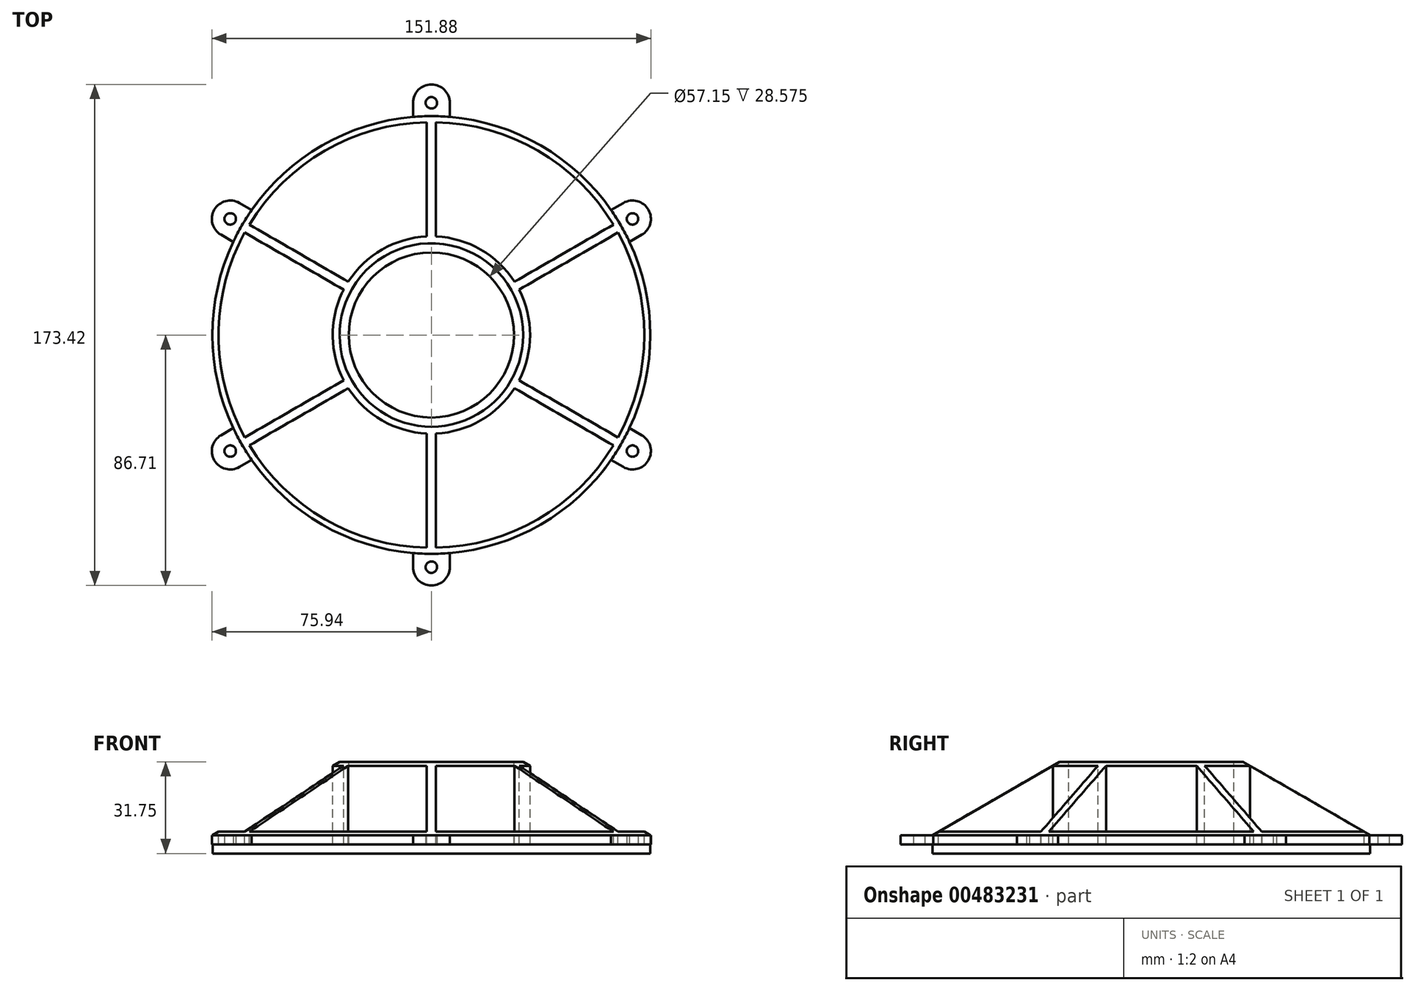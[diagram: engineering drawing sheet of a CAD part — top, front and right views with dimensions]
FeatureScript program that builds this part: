
annotation { "Feature Type Name" : "Feature", "Feature Type Description" : "" }
export const myFeature = defineFeature(function(context is Context, id is Id, definition is map)
    precondition{}
    {
        {
            var Q0;
            Q0=qCreatedBy(makeId("Top.planeOp"),FACE);
            var sketch = newSketch(context, id + "F0", { "sketchPlane" : qUnion([Q0])});
            skCircle(sketch, "E0", {"center": v(0, 0) * mm, "radius": 31.75 * mm});
            skSolve(sketch);
        }
        {
            var Q0;
            Q0 = qSketchRegion(id + "F0", true);
            extrude(context, id + "F1", {"entities" : qUnion([Q0]), "oppositeDirection" : true, "depth" : 25.4 * mm, "hasDraft" : true, "draftAngle" : 60 * degree});
        }
        {
            var Q0;
            Q0=makeQuery(id+"F1.opExtrude","CAP_FACE",FACE,{"disambiguationData":[OSD([sQuery(id+"F0.wireOp",EDGE,"E0")])],"isStart":false});
            var sketch = newSketch(context, id + "F2", { "sketchPlane" : qUnion([Q0])});
            skCircle(sketch, "E1", {"center": v(0, 0) * mm, "radius": 75.74 * mm});
            skSolve(sketch);
        }
        {
            var Q0;
            Q0 = qSketchRegion(id + "F2", true);
            extrude(context, id + "F3", {"entities" : qUnion([Q0]), "operationType" : NewBodyOperationType.ADD, "depth" : 3.17 * mm});
        }
        {
            var Q0;
            Q0=makeQuery(id+"F1.opExtrude","CAP_FACE",FACE,{"disambiguationData":[OSD([sQuery(id+"F0.wireOp",EDGE,"E0")])],"isStart":true});
            var sketch = newSketch(context, id + "F4", { "sketchPlane" : qUnion([Q0])});
            skCircle(sketch, "E2", {"center": v(0, 0) * mm, "radius": 28.58 * mm});
            skSolve(sketch);
        }
        {
            var Q0;
            Q0 = qSketchRegion(id + "F4", true);
            extrude(context, id + "F5", {"entities" : qUnion([Q0]), "operationType" : NewBodyOperationType.REMOVE, "endBound" : BoundingType.THROUGH_ALL, "oppositeDirection" : true, "depth" : 25.4 * mm});
        }
        {
            var Q0;
            Q0=qCreatedBy(makeId("Top.planeOp"),FACE);
            var sketch = newSketch(context, id + "F6", { "sketchPlane" : qUnion([Q0])});
            skCircle(sketch, "E3", {"center": v(0, 0) * mm, "radius": 75.74 * mm, "construction": true});
            skLineSegment(sketch, "E4.0", {"start": v(-75.74, -43.73) * mm, "end": v(-75.74, 43.73) * mm, "construction": true});
            skLineSegment(sketch, "E4.1", {"start": v(-75.74, 43.73) * mm, "end": v(0, 87.46) * mm, "construction": true});
            skLineSegment(sketch, "E4.2", {"start": v(0, 87.46) * mm, "end": v(75.74, 43.73) * mm, "construction": true});
            skLineSegment(sketch, "E4.3", {"start": v(75.74, 43.73) * mm, "end": v(75.74, -43.73) * mm, "construction": true});
            skLineSegment(sketch, "E4.4", {"start": v(75.74, -43.73) * mm, "end": v(0, -87.46) * mm, "construction": true});
            skLineSegment(sketch, "E4.5", {"start": v(0, -87.46) * mm, "end": v(-75.74, -43.73) * mm, "construction": true});
            skPoint(sketch, "E4.0.midPoint", {"position": v(-75.74, 0) * mm});
            skLineSegment(sketch, "E5", {"start": v(0, 0) * mm, "end": v(-75.74, -43.73) * mm, "construction": true});
            skLineSegment(sketch, "E6", {"start": v(0, 0) * mm, "end": v(-75.74, 43.73) * mm, "construction": true});
            skArc(sketch, "E7", {"start": v(-64.57, 35.45) * mm, "mid": v(-73.66, 0) * mm, "end": v(-64.57, -35.45) * mm});
            skArc(sketch, "E8", {"start": v(-30.33, 15.68) * mm, "mid": v(-34.15, 0) * mm, "end": v(-30.33, -15.68) * mm});
            skLineSegment(sketch, "E9.trimOffspring", {"start": v(-30.33, -15.68) * mm, "end": v(-64.57, -35.45) * mm});
            skLineSegment(sketch, "E10.trimOffspring", {"start": v(-30.33, 15.68) * mm, "end": v(-64.57, 35.45) * mm});
            skArc(sketch, "E11.1.0", {"start": v(-28.75, -18.43) * mm, "mid": v(-17.07, -29.57) * mm, "end": v(-1.59, -34.1) * mm});
            skLineSegment(sketch, "E11.1.1", {"start": v(-1.59, -34.1) * mm, "end": v(-1.59, -73.64) * mm});
            skArc(sketch, "E11.1.2", {"start": v(-62.98, -38.2) * mm, "mid": v(-36.83, -63.8) * mm, "end": v(-1.59, -73.64) * mm});
            skLineSegment(sketch, "E11.1.3", {"start": v(-28.75, -18.43) * mm, "end": v(-62.98, -38.2) * mm});
            skArc(sketch, "E11.2.0", {"start": v(1.59, -34.1) * mm, "mid": v(17.07, -29.57) * mm, "end": v(28.75, -18.43) * mm});
            skLineSegment(sketch, "E11.2.1", {"start": v(28.75, -18.43) * mm, "end": v(62.98, -38.2) * mm});
            skArc(sketch, "E11.2.2", {"start": v(1.59, -73.64) * mm, "mid": v(36.83, -63.8) * mm, "end": v(62.98, -38.2) * mm});
            skLineSegment(sketch, "E11.2.3", {"start": v(1.59, -34.1) * mm, "end": v(1.59, -73.64) * mm});
            skArc(sketch, "E11.3.0", {"start": v(30.33, -15.68) * mm, "mid": v(34.15, 0) * mm, "end": v(30.33, 15.68) * mm});
            skLineSegment(sketch, "E11.3.1", {"start": v(30.33, 15.68) * mm, "end": v(64.57, 35.45) * mm});
            skArc(sketch, "E11.3.2", {"start": v(64.57, -35.45) * mm, "mid": v(73.66, 0) * mm, "end": v(64.57, 35.45) * mm});
            skLineSegment(sketch, "E11.3.3", {"start": v(30.33, -15.68) * mm, "end": v(64.57, -35.45) * mm});
            skArc(sketch, "E11.4.0", {"start": v(28.75, 18.43) * mm, "mid": v(17.07, 29.57) * mm, "end": v(1.59, 34.1) * mm});
            skLineSegment(sketch, "E11.4.1", {"start": v(1.59, 34.1) * mm, "end": v(1.59, 73.64) * mm});
            skArc(sketch, "E11.4.2", {"start": v(62.98, 38.2) * mm, "mid": v(36.83, 63.8) * mm, "end": v(1.59, 73.64) * mm});
            skLineSegment(sketch, "E11.4.3", {"start": v(28.75, 18.43) * mm, "end": v(62.98, 38.2) * mm});
            skArc(sketch, "E11.5.0", {"start": v(-1.59, 34.1) * mm, "mid": v(-17.07, 29.57) * mm, "end": v(-28.75, 18.43) * mm});
            skLineSegment(sketch, "E11.5.1", {"start": v(-28.75, 18.43) * mm, "end": v(-62.98, 38.2) * mm});
            skArc(sketch, "E11.5.2", {"start": v(-1.59, 73.64) * mm, "mid": v(-36.83, 63.8) * mm, "end": v(-62.98, 38.2) * mm});
            skLineSegment(sketch, "E11.5.3", {"start": v(-1.59, 34.1) * mm, "end": v(-1.59, 73.64) * mm});
            skSolve(sketch);
        }
        {
            var Q0;
            Q0 = qSketchRegion(id + "F6", true);
            extrude(context, id + "F7", {"entities" : qUnion([Q0]), "operationType" : NewBodyOperationType.REMOVE, "endBound" : BoundingType.THROUGH_ALL, "oppositeDirection" : true, "depth" : 25.4 * mm});
        }
        {
            var Q0;
            Q0=makeQuery(id+"F3.opExtrude","CAP_FACE",FACE,{"disambiguationData":[OSD([sQuery(id+"F2.wireOp",EDGE,"E1")])],"isStart":false});
            var sketch = newSketch(context, id + "F8", { "sketchPlane" : qUnion([Q0])});
            skArc(sketch, "E12", {"start": v(-6.35, -80.36) * mm, "mid": v(0, -86.71) * mm, "end": v(6.35, -80.36) * mm});
            skLineSegment(sketch, "E13", {"start": v(6.35, -80.36) * mm, "end": v(6.35, -75.48) * mm});
            skLineSegment(sketch, "E14", {"start": v(-6.35, -80.36) * mm, "end": v(-6.35, -75.48) * mm});
            skArc(sketch, "E15", {"start": v(6.35, -75.48) * mm, "mid": v(0, -75.74) * mm, "end": v(-6.35, -75.48) * mm});
            skCircle(sketch, "E16", {"center": v(0, -80.36) * mm, "radius": 1.98 * mm});
            skArc(sketch, "E17.1.0", {"start": v(66.42, -45.68) * mm, "mid": v(75.1, -43.36) * mm, "end": v(72.77, -34.68) * mm});
            skLineSegment(sketch, "E17.1.1", {"start": v(72.77, -34.68) * mm, "end": v(68.54, -32.24) * mm});
            skLineSegment(sketch, "E17.1.2", {"start": v(66.42, -45.68) * mm, "end": v(62.2, -43.24) * mm});
            skArc(sketch, "E17.1.3", {"start": v(68.54, -32.24) * mm, "mid": v(65.6, -37.87) * mm, "end": v(62.2, -43.24) * mm});
            skCircle(sketch, "E17.1.4", {"center": v(69.6, -40.18) * mm, "radius": 1.98 * mm});
            skArc(sketch, "E17.2.0", {"start": v(72.77, 34.68) * mm, "mid": v(75.1, 43.36) * mm, "end": v(66.42, 45.68) * mm});
            skLineSegment(sketch, "E17.2.1", {"start": v(66.42, 45.68) * mm, "end": v(62.2, 43.24) * mm});
            skLineSegment(sketch, "E17.2.2", {"start": v(72.77, 34.68) * mm, "end": v(68.54, 32.24) * mm});
            skArc(sketch, "E17.2.3", {"start": v(62.2, 43.24) * mm, "mid": v(65.6, 37.87) * mm, "end": v(68.54, 32.24) * mm});
            skCircle(sketch, "E17.2.4", {"center": v(69.6, 40.18) * mm, "radius": 1.98 * mm});
            skArc(sketch, "E17.3.0", {"start": v(6.35, 80.36) * mm, "mid": v(0, 86.71) * mm, "end": v(-6.35, 80.36) * mm});
            skLineSegment(sketch, "E17.3.1", {"start": v(-6.35, 80.36) * mm, "end": v(-6.35, 75.48) * mm});
            skLineSegment(sketch, "E17.3.2", {"start": v(6.35, 80.36) * mm, "end": v(6.35, 75.48) * mm});
            skArc(sketch, "E17.3.3", {"start": v(-6.35, 75.48) * mm, "mid": v(0, 75.74) * mm, "end": v(6.35, 75.48) * mm});
            skCircle(sketch, "E17.3.4", {"center": v(0, 80.36) * mm, "radius": 1.98 * mm});
            skArc(sketch, "E17.4.0", {"start": v(-66.42, 45.68) * mm, "mid": v(-75.1, 43.36) * mm, "end": v(-72.77, 34.68) * mm});
            skLineSegment(sketch, "E17.4.1", {"start": v(-72.77, 34.68) * mm, "end": v(-68.54, 32.24) * mm});
            skLineSegment(sketch, "E17.4.2", {"start": v(-66.42, 45.68) * mm, "end": v(-62.2, 43.24) * mm});
            skArc(sketch, "E17.4.3", {"start": v(-68.54, 32.24) * mm, "mid": v(-65.6, 37.87) * mm, "end": v(-62.2, 43.24) * mm});
            skCircle(sketch, "E17.4.4", {"center": v(-69.6, 40.18) * mm, "radius": 1.98 * mm});
            skArc(sketch, "E17.5.0", {"start": v(-72.77, -34.68) * mm, "mid": v(-75.1, -43.36) * mm, "end": v(-66.42, -45.68) * mm});
            skLineSegment(sketch, "E17.5.1", {"start": v(-66.42, -45.68) * mm, "end": v(-62.2, -43.24) * mm});
            skLineSegment(sketch, "E17.5.2", {"start": v(-72.77, -34.68) * mm, "end": v(-68.54, -32.24) * mm});
            skArc(sketch, "E17.5.3", {"start": v(-62.2, -43.24) * mm, "mid": v(-65.6, -37.87) * mm, "end": v(-68.54, -32.24) * mm});
            skCircle(sketch, "E17.5.4", {"center": v(-69.6, -40.18) * mm, "radius": 1.98 * mm});
            skSolve(sketch);
        }
        {
            var Q0;
            Q0 = qSketchRegion(id + "F8", true);
            extrude(context, id + "F9", {"entities" : qUnion([Q0]), "operationType" : NewBodyOperationType.ADD, "oppositeDirection" : true, "depth" : 3.17 * mm});
        }
        {
            var Q0;
            Q0=makeQuery(id+"F9.boolean.opBoolean","MERGE",FACE,{"derivedFrom":[makeQuery(id+"F3.opExtrude","CAP_FACE",FACE,{"disambiguationData":[OSD([sQuery(id+"F2.wireOp",EDGE,"E1")])],"isStart":false}),makeQuery(id+"F9.opExtrude","CAP_FACE",FACE,{"disambiguationData":[OSD([sQuery(id+"F8.wireOp",EDGE,"E12"),sQuery(id+"F8.wireOp",EDGE,"E13"),sQuery(id+"F8.wireOp",EDGE,"E14"),sQuery(id+"F8.wireOp",EDGE,"E15"),sQuery(id+"F8.wireOp",EDGE,"E16")])],"isStart":true}),makeQuery(id+"F9.opExtrude","CAP_FACE",FACE,{"disambiguationData":[OSD([sQuery(id+"F8.wireOp",EDGE,"E17.1.0"),sQuery(id+"F8.wireOp",EDGE,"E17.1.1"),sQuery(id+"F8.wireOp",EDGE,"E17.1.2"),sQuery(id+"F8.wireOp",EDGE,"E17.1.3"),sQuery(id+"F8.wireOp",EDGE,"E17.1.4")])],"isStart":true}),makeQuery(id+"F9.opExtrude","CAP_FACE",FACE,{"disambiguationData":[OSD([sQuery(id+"F8.wireOp",EDGE,"E17.2.0"),sQuery(id+"F8.wireOp",EDGE,"E17.2.1"),sQuery(id+"F8.wireOp",EDGE,"E17.2.2"),sQuery(id+"F8.wireOp",EDGE,"E17.2.3"),sQuery(id+"F8.wireOp",EDGE,"E17.2.4")])],"isStart":true}),makeQuery(id+"F9.opExtrude","CAP_FACE",FACE,{"disambiguationData":[OSD([sQuery(id+"F8.wireOp",EDGE,"E17.3.0"),sQuery(id+"F8.wireOp",EDGE,"E17.3.1"),sQuery(id+"F8.wireOp",EDGE,"E17.3.2"),sQuery(id+"F8.wireOp",EDGE,"E17.3.3"),sQuery(id+"F8.wireOp",EDGE,"E17.3.4")])],"isStart":true}),makeQuery(id+"F9.opExtrude","CAP_FACE",FACE,{"disambiguationData":[OSD([sQuery(id+"F8.wireOp",EDGE,"E17.4.0"),sQuery(id+"F8.wireOp",EDGE,"E17.4.1"),sQuery(id+"F8.wireOp",EDGE,"E17.4.2"),sQuery(id+"F8.wireOp",EDGE,"E17.4.3"),sQuery(id+"F8.wireOp",EDGE,"E17.4.4")])],"isStart":true}),makeQuery(id+"F9.opExtrude","CAP_FACE",FACE,{"disambiguationData":[OSD([sQuery(id+"F8.wireOp",EDGE,"E17.5.0"),sQuery(id+"F8.wireOp",EDGE,"E17.5.1"),sQuery(id+"F8.wireOp",EDGE,"E17.5.2"),sQuery(id+"F8.wireOp",EDGE,"E17.5.3"),sQuery(id+"F8.wireOp",EDGE,"E17.5.4")])],"isStart":true})]});
            var sketch = newSketch(context, id + "F10", { "sketchPlane" : qUnion([Q0])});
            skCircle(sketch, "E18", {"center": v(0, 0) * mm, "radius": 75.7 * mm});
            skSolve(sketch);
        }
        {
            var Q0;
            Q0 = qSketchRegion(id + "F10", true);
            extrude(context, id + "F11", {"entities" : qUnion([Q0]), "depth" : 3.17 * mm});
        }
    });
